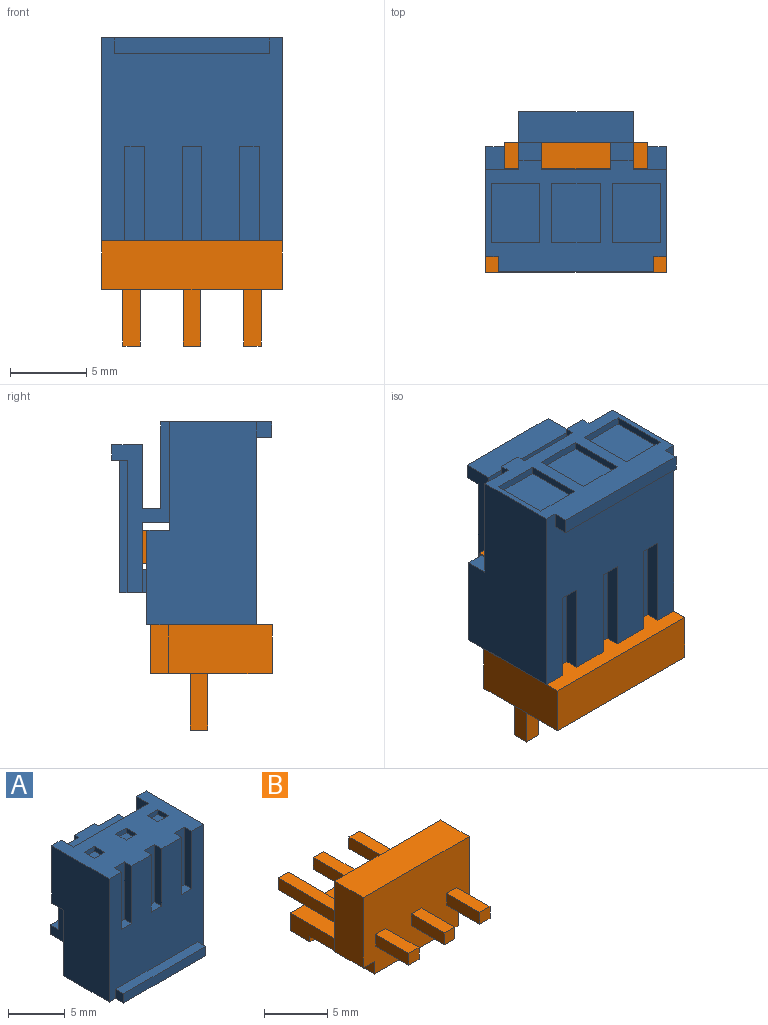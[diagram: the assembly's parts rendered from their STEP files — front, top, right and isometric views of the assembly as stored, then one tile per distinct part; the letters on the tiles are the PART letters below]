
ASSEMBLY  parts=2 mates=1
PART A: 82 faces, bbox 11.8x10.5x13.3 mm
  f0: plane 3.9x0.5mm, normal (1,0,0), area 1.9mm2, adj f1,f2,f3,f4
  f1: plane 3.15x0.5mm, normal (0,1,0), area 1.6mm2, adj f0,f2,f3,f5
  f2: plane 11.82x7.3mm, normal (0,0,-1), area 42.5mm2, adj f0,f1,f4,f5,f6,f7,f8,f9
  f3: plane 3.9x3.15mm, normal (0,0,-1), area 12.3mm2, adj f0,f1,f4,f5
  f4: plane 3.15x0.5mm, normal (0,-1,0), area 1.6mm2, adj f0,f2,f3,f5
  f5: plane 3.9x0.5mm, normal (-1,0,0), area 1.9mm2, adj f1,f2,f3,f4
  f6: plane 6.6x1.8mm, normal (1,0,0), area 5mm2, adj f2,f7,f22,f27,f28,f29
  f7: plane 13.3x11.82mm, normal (0,1,0), area 122.5mm2, adj f2,f6,f9,f10,f15,f17,f20,f29
  f8: plane 3.15x0.5mm, normal (0,1,0), area 1.6mm2, adj f2,f21,f26,f36
  f9: plane 6.6x1.8mm, normal (-1,0,0), area 5mm2, adj f2,f7,f18,f28,f32,f37
  f10: plane 11.2x3.8mm, normal (-1,0,0), area 15.7mm2, adj f2,f7,f22,f27,f28,f29,f38,f39
  f11: plane 3.15x0.5mm, normal (0,-1,0), area 1.6mm2, adj f2,f19,f25,f43
  f12: plane 3.15x0.5mm, normal (0,-1,0), area 1.6mm2, adj f2,f21,f26,f36
  f13: plane 1x1mm, normal (-1,0,0), area 1mm2, adj f2,f16,f23,f44
  f14: plane 1x1mm, normal (1,0,0), area 1mm2, adj f2,f16,f23,f44
  f15: plane 13.3x7.2mm, normal (-1,0,0), area 85.1mm2, adj f2,f7,f23,f31,f33,f45
  f16: plane 10.22x1mm, normal (0,-1,0), area 10.2mm2, adj f2,f13,f14,f44
  f17: plane 11.2x3.8mm, normal (1,0,0), area 15.7mm2, adj f2,f7,f18,f28,f32,f37,f38,f39
  f18: plane 5.7x1.5mm, normal (0,1,0), area 8.5mm2, adj f2,f9,f17,f37
  f19: plane 3.9x0.5mm, normal (-1,0,0), area 1.9mm2, adj f2,f11,f24,f43
  f20: plane 13.3x7.2mm, normal (1,0,0), area 85.1mm2, adj f2,f7,f23,f30,f33,f47
  f21: plane 3.9x0.5mm, normal (-1,0,0), area 1.9mm2, adj f2,f8,f12,f36
  f22: plane 5.7x1.5mm, normal (0,1,0), area 8.5mm2, adj f2,f6,f10,f27
  f23: plane 13.3x11.82mm, normal (0,-1,0), area 122.8mm2, adj f2,f13,f14,f15,f20,f33,f44,f48
  f24: plane 3.15x0.5mm, normal (0,1,0), area 1.6mm2, adj f2,f19,f25,f43
  f25: plane 3.9x0.5mm, normal (1,0,0), area 1.9mm2, adj f2,f11,f24,f43
  f26: plane 3.9x0.5mm, normal (1,0,0), area 1.9mm2, adj f2,f8,f12,f36
  f27: plane 1.5x1.2mm, normal (0,0,-1), area 1.8mm2, adj f6,f10,f22,f28
  f28: plane 9.7x7.5mm, normal (0,-1,0), area 63.3mm2, adj f6,f9,f10,f17,f27,f29,f32,f37
  f29: plane 1.8x1.5mm, normal (0,0,1), area 2.7mm2, adj f6,f7,f10,f28
  f30: plane 1.5x1.2mm, normal (0,0,-1), area 1.8mm2, adj f7,f20,f34,f47
  f31: plane 1.5x1.2mm, normal (0,0,-1), area 1.8mm2, adj f7,f15,f35,f45
  f32: plane 1.8x1.5mm, normal (0,0,1), area 2.7mm2, adj f7,f9,f17,f28
  f33: plane 11.82x7.2mm, normal (0,0,1), area 62.4mm2, adj f7,f15,f20,f23,f34,f35,f45,f47
  f34: plane 6.2x1.5mm, normal (-1,0,0), area 9.3mm2, adj f7,f30,f33,f47
  f35: plane 6.2x1.5mm, normal (1,0,0), area 9.3mm2, adj f7,f31,f33,f45
  f36: plane 3.9x3.15mm, normal (0,0,-1), area 12.3mm2, adj f8,f12,f21,f26
  f37: plane 1.5x1.2mm, normal (0,0,-1), area 1.8mm2, adj f9,f17,f18,f28
  f38: plane 7.5x1mm, normal (0,1,0), area 7.5mm2, adj f10,f17,f39,f41
  f39: plane 7.5x1mm, normal (0,0,1), area 6.3mm2, adj f10,f17,f38,f42,f46,f75,f76,f77
  f40: plane 7.5x2.1mm, normal (0,0,1), area 11.5mm2, adj f10,f17,f28,f42,f46,f57,f58,f75
  f41: plane 7.5x2mm, normal (0,0,-1), area 15mm2, adj f10,f17,f28,f38
  f42: plane 8.7x2.5mm, normal (0,1,0), area 21.8mm2, adj f10,f39,f40,f75
  f43: plane 3.9x3.15mm, normal (0,0,-1), area 12.3mm2, adj f11,f19,f24,f25
  f44: plane 10.22x1mm, normal (0,0,1), area 10.2mm2, adj f13,f14,f16,f23
  f45: plane 6.2x1.2mm, normal (0,1,0), area 7.4mm2, adj f15,f31,f33,f35
  f46: plane 8.7x2.5mm, normal (0,1,0), area 21.7mm2, adj f17,f39,f40,f76
  f47: plane 6.2x1.2mm, normal (0,1,0), area 7.4mm2, adj f20,f30,f33,f34
  f48: plane 6.2x0.9mm, normal (-1,0,0), area 5.6mm2, adj f23,f33,f49,f73
  f49: plane 1.3x0.9mm, normal (0,0,1), area 1.2mm2, adj f23,f48,f56,f73
  f50: plane 1.3x0.9mm, normal (0,0,1), area 1.2mm2, adj f23,f53,f55,f71
  f51: plane 1.3x0.9mm, normal (0,0,1), area 1.2mm2, adj f23,f52,f54,f62
  f52: plane 6.2x0.9mm, normal (-1,0,0), area 5.6mm2, adj f23,f33,f51,f62
  f53: plane 6.2x0.9mm, normal (-1,0,0), area 5.6mm2, adj f23,f33,f50,f71
  f54: plane 6.2x0.9mm, normal (1,0,0), area 5.6mm2, adj f23,f33,f51,f62
  f55: plane 6.2x0.9mm, normal (1,0,0), area 5.6mm2, adj f23,f33,f50,f71
  f56: plane 6.2x0.9mm, normal (1,0,0), area 5.6mm2, adj f23,f33,f49,f73
  f57: plane 1.5x0.6mm, normal (1,0,0), area 0.9mm2, adj f28,f40,f59,f78
  f58: plane 1.5x0.6mm, normal (-1,0,0), area 0.9mm2, adj f28,f40,f59,f78
  f59: plane 4.5x0.6mm, normal (0,0,-1), area 2.7mm2, adj f28,f57,f58,f78
  f60: plane 1.3x0.5mm, normal (0,-1,0), area 0.6mm2, adj f33,f61,f70,f79
  f61: plane 1.3x0.5mm, normal (1,0,0), area 0.6mm2, adj f33,f60,f72,f79
  f62: plane 6.2x1.3mm, normal (0,-1,0), area 8.1mm2, adj f33,f51,f52,f54
  f63: plane 1.3x0.5mm, normal (0,1,0), area 0.6mm2, adj f33,f69,f74,f80
  f64: plane 1.3x0.5mm, normal (-1,0,0), area 0.6mm2, adj f33,f66,f67,f81
  f65: plane 1.3x0.5mm, normal (0,-1,0), area 0.6mm2, adj f33,f69,f74,f80
  f66: plane 1.3x0.5mm, normal (0,1,0), area 0.6mm2, adj f33,f64,f68,f81
  f67: plane 1.3x0.5mm, normal (0,-1,0), area 0.6mm2, adj f33,f64,f68,f81
  f68: plane 1.3x0.5mm, normal (1,0,0), area 0.6mm2, adj f33,f66,f67,f81
  f69: plane 1.3x0.5mm, normal (1,0,0), area 0.6mm2, adj f33,f63,f65,f80
  f70: plane 1.3x0.5mm, normal (-1,0,0), area 0.6mm2, adj f33,f60,f72,f79
  f71: plane 6.2x1.3mm, normal (0,-1,0), area 8.1mm2, adj f33,f50,f53,f55
  f72: plane 1.3x0.5mm, normal (0,1,0), area 0.6mm2, adj f33,f61,f70,f79
  f73: plane 6.2x1.3mm, normal (0,-1,0), area 8.1mm2, adj f33,f48,f49,f56
  f74: plane 1.3x0.5mm, normal (-1,0,0), area 0.6mm2, adj f33,f63,f65,f80
  f75: plane 8.7x0.5mm, normal (-1,0,0), area 4.3mm2, adj f39,f40,f42,f77
  f76: plane 8.7x0.5mm, normal (1,0,0), area 4.3mm2, adj f39,f40,f46,f77
  f77: plane 8.7x2.5mm, normal (0,1,0), area 21.8mm2, adj f39,f40,f75,f76
  f78: plane 4.5x1.5mm, normal (0,-1,0), area 6.8mm2, adj f40,f57,f58,f59
  f79: plane 1.3x1.3mm, normal (0,0,1), area 1.7mm2, adj f60,f61,f70,f72
  f80: plane 1.3x1.3mm, normal (0,0,1), area 1.7mm2, adj f63,f65,f69,f74
  f81: plane 1.3x1.3mm, normal (0,0,1), area 1.7mm2, adj f64,f66,f67,f68
PART B: 44 faces, bbox 11.8x14.6x8.5 mm
  f0: plane 7.7x1.14mm, normal (0,0,1), area 8.8mm2, adj f1,f2,f3,f4
  f1: plane 11.82x6.8mm, normal (0,1,0), area 76.5mm2, adj f0,f2,f4,f5,f6,f7,f8,f9
  f2: plane 7.7x1.14mm, normal (-1,0,0), area 8.8mm2, adj f0,f1,f3,f7
  f3: plane 1.14x1.14mm, normal (0,1,0), area 1.3mm2, adj f0,f2,f4,f7
  f4: plane 7.7x1.14mm, normal (1,0,0), area 8.8mm2, adj f0,f1,f3,f7
  f5: plane 7.7x1.14mm, normal (0,0,-1), area 8.8mm2, adj f1,f11,f19,f20
  f6: plane 6.8x3.2mm, normal (-1,0,0), area 21.8mm2, adj f1,f9,f17,f21
  f7: plane 7.7x1.14mm, normal (0,0,-1), area 8.8mm2, adj f1,f2,f3,f4
  f8: plane 6.8x3.2mm, normal (1,0,0), area 21.8mm2, adj f1,f9,f10,f21
  f9: plane 11.82x3.2mm, normal (0,0,1), area 37.8mm2, adj f1,f6,f8,f21
  f10: plane 3.2x1.25mm, normal (0,0,-1), area 4mm2, adj f1,f8,f21,f22
  f11: plane 7.7x1.14mm, normal (-1,0,0), area 8.8mm2, adj f1,f5,f18,f20
  f12: plane 9.32x6.2mm, normal (0,0,1), area 57.8mm2, adj f1,f22,f23,f24
  f13: plane 7.7x1.14mm, normal (-1,0,0), area 8.8mm2, adj f1,f15,f16,f25
  f14: plane 7.7x1.14mm, normal (1,0,0), area 8.8mm2, adj f1,f15,f16,f25
  f15: plane 7.7x1.14mm, normal (0,0,-1), area 8.8mm2, adj f1,f13,f14,f25
  f16: plane 7.7x1.14mm, normal (0,0,1), area 8.8mm2, adj f1,f13,f14,f25
  f17: plane 3.2x1.25mm, normal (0,0,-1), area 4mm2, adj f1,f6,f21,f24
  f18: plane 7.7x1.14mm, normal (0,0,1), area 8.8mm2, adj f1,f11,f19,f20
  f19: plane 7.7x1.14mm, normal (1,0,0), area 8.8mm2, adj f1,f5,f18,f20
  f20: plane 1.14x1.14mm, normal (0,1,0), area 1.3mm2, adj f5,f11,f18,f19
  f21: plane 11.82x8mm, normal (0,-1,0), area 87.7mm2, adj f6,f8,f9,f10,f17,f22,f24,f26
  f22: plane 9.4x1.7mm, normal (1,0,0), area 12.4mm2, adj f10,f12,f21,f23,f30,f39,f40
  f23: plane 9.32x1.7mm, normal (0,1,0), area 15.8mm2, adj f12,f22,f24,f40
  f24: plane 9.4x1.7mm, normal (-1,0,0), area 12.4mm2, adj f12,f17,f21,f23,f30,f39,f40
  f25: plane 1.14x1.14mm, normal (0,1,0), area 1.3mm2, adj f13,f14,f15,f16
  f26: plane 3.7x1.14mm, normal (0,0,-1), area 4.2mm2, adj f21,f28,f31,f41
  f27: plane 3.7x1.14mm, normal (1,0,0), area 4.2mm2, adj f21,f34,f38,f42
  f28: plane 3.7x1.14mm, normal (-1,0,0), area 4.2mm2, adj f21,f26,f36,f41
  f29: plane 3.7x1.14mm, normal (-1,0,0), area 4.2mm2, adj f21,f34,f38,f42
  f30: plane 9.32x7.2mm, normal (0,0,-1), area 67.1mm2, adj f21,f22,f24,f39
  f31: plane 3.7x1.14mm, normal (1,0,0), area 4.2mm2, adj f21,f26,f36,f41
  f32: plane 3.7x1.14mm, normal (0,0,-1), area 4.2mm2, adj f21,f33,f35,f43
  f33: plane 3.7x1.14mm, normal (-1,0,0), area 4.2mm2, adj f21,f32,f37,f43
  f34: plane 3.7x1.14mm, normal (0,0,-1), area 4.2mm2, adj f21,f27,f29,f42
  f35: plane 3.7x1.14mm, normal (1,0,0), area 4.2mm2, adj f21,f32,f37,f43
  f36: plane 3.7x1.14mm, normal (0,0,1), area 4.2mm2, adj f21,f28,f31,f41
  f37: plane 3.7x1.14mm, normal (0,0,1), area 4.2mm2, adj f21,f33,f35,f43
  f38: plane 3.7x1.14mm, normal (0,0,1), area 4.2mm2, adj f21,f27,f29,f42
  f39: plane 9.32x0.5mm, normal (0,-1,0), area 4.7mm2, adj f22,f24,f30,f40
  f40: plane 9.32x2.2mm, normal (0,0,-1), area 20.5mm2, adj f22,f23,f24,f39
  f41: plane 1.14x1.14mm, normal (0,-1,0), area 1.3mm2, adj f26,f28,f31,f36
  f42: plane 1.14x1.14mm, normal (0,-1,0), area 1.3mm2, adj f27,f29,f34,f38
  f43: plane 1.14x1.14mm, normal (0,-1,0), area 1.3mm2, adj f32,f33,f35,f37
PLACE A rot(axis=(0,1,0),180deg) t=(5.91,1.01,9.85)mm
PLACE B rot(axis=(1,0,0),90deg) t=(5.91,4.25,0)mm
MATE fastened A.f33 <-> B.f1  axis (0,0,-1) through (5.91,4.13,3.2)mm
